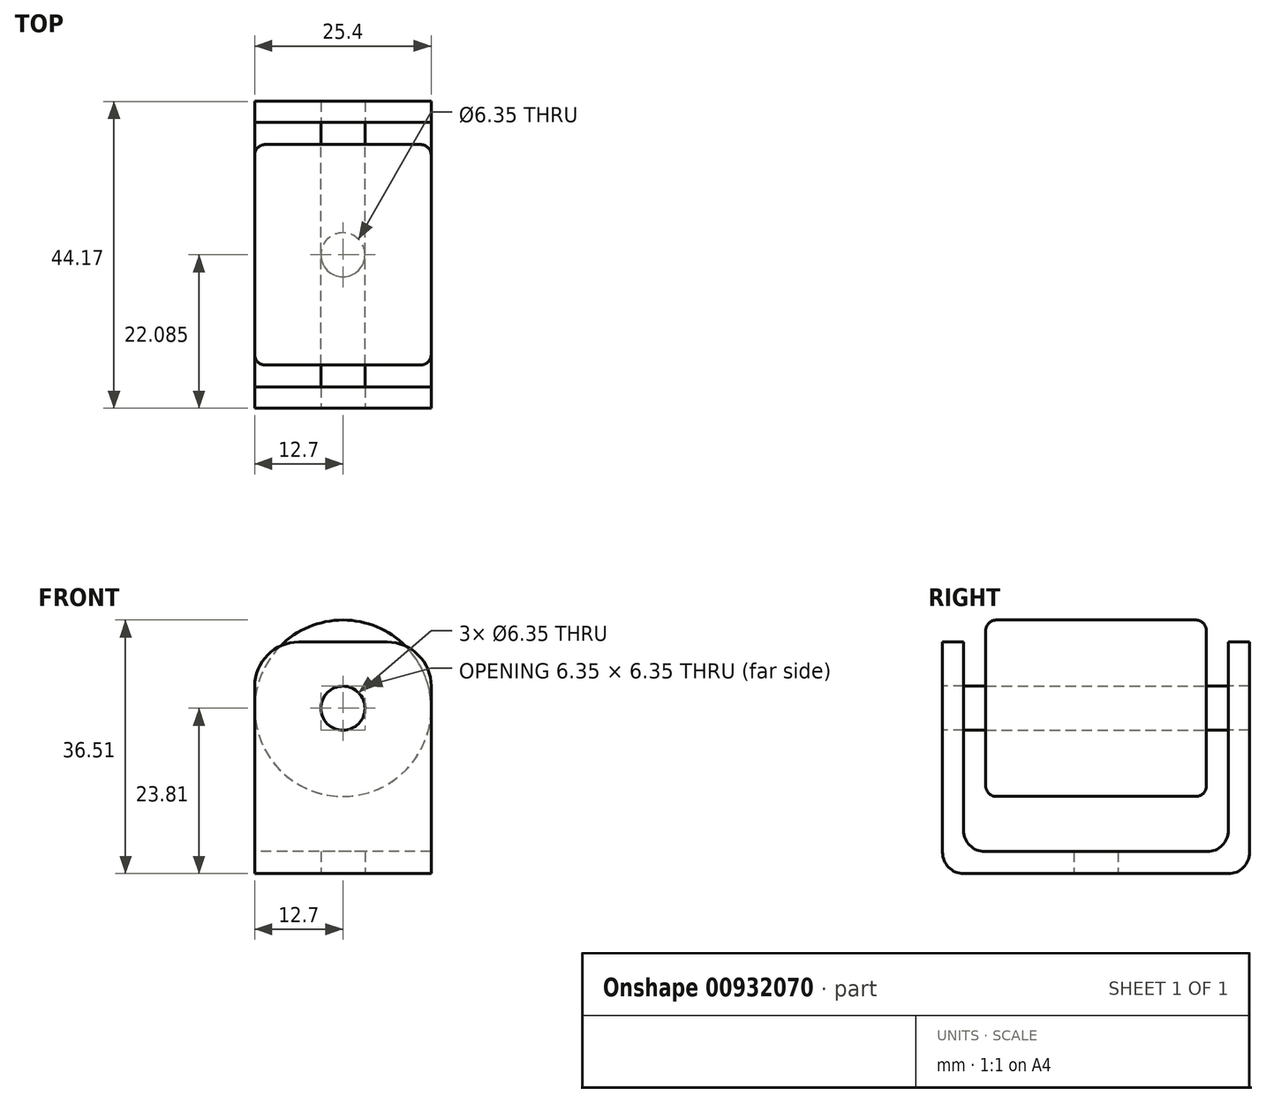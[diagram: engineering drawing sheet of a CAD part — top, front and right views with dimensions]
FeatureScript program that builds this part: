
annotation { "Feature Type Name" : "Feature", "Feature Type Description" : "" }
export const myFeature = defineFeature(function(context is Context, id is Id, definition is map)
    precondition{}
    {
        {
            var Q0;
            Q0=qCreatedBy(makeId("Front.planeOp"),FACE);
            var sketch = newSketch(context, id + "F0", { "sketchPlane" : qUnion([Q0])});
            skCircle(sketch, "E0", {"center": v(0, 0) * mm, "radius": 3.18 * mm});
            skCircle(sketch, "E1", {"center": v(0, 0) * mm, "radius": 12.7 * mm});
            skSolve(sketch);
        }
        {
            var Q0;
            Q0 = qSketchRegion(id + "F0", true);
            extrude(context, id + "F1", {"entities" : qUnion([Q0]), "depth" : 31.75 * mm, "offsetDistance" : 25.4 * mm});
        }
        {
            var Q0;
            Q0=qCreatedBy(makeId("Right.planeOp"),FACE);
            var sketch = newSketch(context, id + "F2", { "sketchPlane" : qUnion([Q0])});
            skLineSegment(sketch, "E2", {"start": v(-34.92, 9.53) * mm, "end": v(-34.92, -20.64) * mm});
            skLineSegment(sketch, "E3", {"start": v(-34.92, -20.64) * mm, "end": v(3.18, -20.64) * mm});
            skLineSegment(sketch, "E4", {"start": v(3.18, -20.64) * mm, "end": v(3.18, 9.53) * mm});
            skLineSegment(sketch, "E5", {"start": v(3.17, 9.53) * mm, "end": v(6.21, 9.53) * mm});
            skLineSegment(sketch, "E6", {"start": v(6.21, 9.53) * mm, "end": v(6.21, -23.81) * mm});
            skLineSegment(sketch, "E7", {"start": v(6.21, -23.81) * mm, "end": v(-37.96, -23.81) * mm});
            skLineSegment(sketch, "E8", {"start": v(-37.96, -23.81) * mm, "end": v(-37.96, 9.53) * mm});
            skLineSegment(sketch, "E9", {"start": v(-37.96, 9.53) * mm, "end": v(-34.92, 9.53) * mm});
            skLineSegment(sketch, "E10", {"start": v(0, -12.7) * mm, "end": v(-31.75, -12.7) * mm, "construction": true});
            skSolve(sketch);
        }
        {
            var Q0;
            Q0 = qSketchRegion(id + "F2", true);
            extrude(context, id + "F3", {"entities" : qUnion([Q0]), "depth" : 12.7 * mm, "offsetDistance" : 25.4 * mm, "hasSecondDirection" : true, "secondDirectionOppositeDirection" : true, "secondDirectionDepth" : 12.7 * mm});
        }
        {
            var Q0;
            Q0=makeQuery(id+"F3.opExtrude","SWEPT_EDGE",EDGE,{"disambiguationData":[OSD([sQuery(id+"F2.wireOp",EDGE,"E7"),sQuery(id+"F2.wireOp",EDGE,"E8")])]});
            var Q1;
            Q1=makeQuery(id+"F3.opExtrude","SWEPT_EDGE",EDGE,{"disambiguationData":[OSD([sQuery(id+"F2.wireOp",EDGE,"E2"),sQuery(id+"F2.wireOp",EDGE,"E3")])]});
            var Q2;
            Q2=makeQuery(id+"F3.opExtrude","SWEPT_EDGE",EDGE,{"disambiguationData":[OSD([sQuery(id+"F2.wireOp",EDGE,"E3"),sQuery(id+"F2.wireOp",EDGE,"E4")])]});
            var Q3;
            Q3=makeQuery(id+"F3.opExtrude","SWEPT_EDGE",EDGE,{"disambiguationData":[OSD([sQuery(id+"F2.wireOp",EDGE,"E6"),sQuery(id+"F2.wireOp",EDGE,"E7")])]});
            fillet(context, id + "F4", {"entities" : qUnion([Q0, Q1, Q2, Q3]), "radius" : 3.05 * mm, "tangentPropagation" : true, "allowEdgeOverflow" : false});
        }
        {
            var Q0;
            Q0=makeQuery(id+"F3.opExtrude","CAP_EDGE",EDGE,{"disambiguationData":[OSD([sQuery(id+"F2.wireOp",EDGE,"E9")])],"isStart":false});
            var Q1;
            Q1=makeQuery(id+"F3.opExtrude","CAP_EDGE",EDGE,{"disambiguationData":[OSD([sQuery(id+"F2.wireOp",EDGE,"E9")])],"isStart":true});
            var Q2;
            Q2=makeQuery(id+"F3.opExtrude","CAP_EDGE",EDGE,{"disambiguationData":[OSD([sQuery(id+"F2.wireOp",EDGE,"E5")])],"isStart":true});
            var Q3;
            Q3=makeQuery(id+"F3.opExtrude","CAP_EDGE",EDGE,{"disambiguationData":[OSD([sQuery(id+"F2.wireOp",EDGE,"E5")])],"isStart":false});
            fillet(context, id + "F5", {"entities" : qUnion([Q0, Q1, Q2, Q3]), "radius" : 6.35 * mm, "tangentPropagation" : true, "allowEdgeOverflow" : false});
        }
        {
            var Q0;
            Q0=makeQuery(id+"F3.opExtrude","SWEPT_FACE",FACE,{"disambiguationData":[OSD([sQuery(id+"F2.wireOp",EDGE,"E8")])]});
            var sketch = newSketch(context, id + "F6", { "sketchPlane" : qUnion([Q0])});
            skCircle(sketch, "E11.0", {"center": v(0, 0) * mm, "radius": 3.18 * mm});
            skSolve(sketch);
        }
        {
            var Q0;
            Q0 = qSketchRegion(id + "F6", true);
            extrude(context, id + "F7", {"entities" : qUnion([Q0]), "operationType" : NewBodyOperationType.REMOVE, "endBound" : BoundingType.THROUGH_ALL, "oppositeDirection" : true, "depth" : 25.4 * mm, "offsetDistance" : 25.4 * mm});
        }
        {
            var Q0;
            Q0=makeQuery(id+"F3.opExtrude","SWEPT_FACE",FACE,{"disambiguationData":[OSD([sQuery(id+"F2.wireOp",EDGE,"E8")])]});
            var sketch = newSketch(context, id + "F8", { "sketchPlane" : qUnion([Q0])});
            skCircle(sketch, "E12", {"center": v(0, 0) * mm, "radius": 3.18 * mm});
            skSolve(sketch);
        }
        {
            var Q0;
            Q0 = qSketchRegion(id + "F8", true);
            var Q1;
            Q1=makeQuery(id+"F3.opExtrude","SWEPT_FACE",FACE,{"disambiguationData":[OSD([sQuery(id+"F2.wireOp",EDGE,"E6")])]});
            extrude(context, id + "F9", {"entities" : qUnion([Q0]), "endBound" : BoundingType.UP_TO_SURFACE, "oppositeDirection" : true, "depth" : 25.4 * mm, "endBoundEntityFace" : qUnion([Q1]), "offsetDistance" : 25.4 * mm});
        }
        {
            var Q0;
            Q0=makeQuery(id+"F3.opExtrude","SWEPT_FACE",FACE,{"disambiguationData":[OSD([sQuery(id+"F2.wireOp",EDGE,"E7")])]});
            var sketch = newSketch(context, id + "F10", { "sketchPlane" : qUnion([Q0])});
            skCircle(sketch, "E13", {"center": v(0, 15.88) * mm, "radius": 3.18 * mm});
            skLineSegment(sketch, "E14", {"start": v(0, 15.88) * mm, "end": v(0, 34.91) * mm, "construction": true});
            skLineSegment(sketch, "E15", {"start": v(0, 15.88) * mm, "end": v(0, -3.16) * mm, "construction": true});
            skSolve(sketch);
        }
        {
            var Q0;
            Q0 = qSketchRegion(id + "F10", true);
            var Q1;
            Q1=makeQuery(id+"F3.opExtrude","SWEPT_FACE",FACE,{"disambiguationData":[OSD([sQuery(id+"F2.wireOp",EDGE,"E3")])]});
            extrude(context, id + "F11", {"entities" : qUnion([Q0]), "operationType" : NewBodyOperationType.REMOVE, "endBound" : BoundingType.UP_TO_SURFACE, "oppositeDirection" : true, "depth" : 25.4 * mm, "endBoundEntityFace" : qUnion([Q1]), "offsetDistance" : 25.4 * mm});
        }
        {
            var Q0;
            Q0=makeQuery(id+"F1.opExtrude","CAP_EDGE",EDGE,{"disambiguationData":[OSD([sQuery(id+"F0.wireOp",EDGE,"E1")])],"isStart":false});
            var Q1;
            Q1=makeQuery(id+"F1.opExtrude","CAP_EDGE",EDGE,{"disambiguationData":[OSD([sQuery(id+"F0.wireOp",EDGE,"E1")])],"isStart":true});
            fillet(context, id + "F12", {"entities" : qUnion([Q0, Q1]), "radius" : 1.52 * mm, "tangentPropagation" : true, "allowEdgeOverflow" : false});
        }
    });
